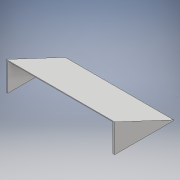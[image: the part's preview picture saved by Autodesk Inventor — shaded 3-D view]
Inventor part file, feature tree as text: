
AUTODESK INVENTOR PART (.ipt)
format: ipt  version: 2018.2 (Build 222227000, 227)  size: 126,464 bytes
history: native  units: mm
features: extrude x4, sketch x4
ambient origin geometry x8: Origin, YZ Plane, XZ Plane, XY Plane, X Axis, Y Axis, Z Axis, Center Point
bodies: Solid1 (feature_tree)
feature tree (8):
  extrude  "Extrusion1"  Depth=156.0mm
  extrude  "Extrusion2"  Depth=82.6mm
  extrude  "Extrusion3"  Depth=151.2mm TaperAngle=0.0deg
  extrude  "Extrusion5"  Depth=2.4mm TaperAngle=0.0deg
  sketch  "Sketch1"  dims[d0=85.0mm d1=156.0mm]
  sketch  "Sketch2"  dims[d2=2.4mm d3=82.6mm]
  sketch  "Sketch3"  dims[d4=151.2mm d5=0.9mm d6=0.0mm]
  sketch  "Sketch5"  dims[d7=40.0mm d8=2.4mm d9=0.0mm d10=2.4mm d11=0.0mm d18=152.0mm d19=0.0mm]
